# Revit family: Door_Sliding_AssaAbloy_Resilience-FBO-Single-MS
name_source: partatom
category: Doors
revit_build: Autodesk Revit 2016 (Build: 20150714_1515(x64)
units: mm (PartAtom-declared; Revit-internal decimal feet)

## family parameters
Always vertical = Yes
Cut with Voids When Loaded = No
Host = Wall
OmniClass Number = 23.30.10.17.11
OmniClass Title = Sliding Doors
Room Calculation Point = No
Shared = No

## types (14) — shared parameters
AAMA Designation = DP 80
Analytic Construction = <None>
Assembly Code = B2030110
Exit Device Height = 3' - 0"
Fire Rating = As Specified
Fixed Sidelight = Yes
Frame Depth = 0' - 4 1/2"
Full Breakout = No
Function = Interior
Heat Transfer Coefficient (U) = 0.1 BTU/(h·ft²·°F)
Jamb Width = 0' - 1 3/4"
Keynote = 08463
Manufacturer = ASSA ABLOY Entrance Systems
Maximum Size = 86 W x 90 H -- 108 W x 104 H
Medium Stile = Yes
Muntin Width Options = 1-3/4'', 4''
Narrow Stile = No
Panel Thickness = 0' - 1 3/4"
R = 0.0000 (h·ft²·°F)/BTU
RO Offset = 0' - 0 1/4"
Stile Width = 0' - 4"
Thermal Resistance (R) = 0.0000 (h·ft²·°F)/BTU
Thickness = 0' - 0"
U = 0.1 BTU/(h·ft²·°F)
URL = https://www.assaabloyentrance.us
Wall Closure = By host
Water Penetration = NOT TESTED OR RATED for Water Infiltration
zero-valued in all types: Expected Lifespan (Years), Maintenance Schedule (Months), SHGC, Solar Heat Gain Coefficient, VLT, Visual Light Transmittance, Warranty Duration (Years)

## per-type parameters (varying)
| type | Description | Include Muntin A | Include Muntin B | Include Muntin C | Model | Muntin Width | Standards Conformance |
| Category D - No Muntins | ASSA ABLOY Automatic Impact Rated Sliding Door - SL500 Resilience R104 D as Specified | No | No | No | ASSA ABLOY SS SL500 Resilience R104 D Medium Stile | 0' - 1 3/4" | State of Florida FL26008  ;  Category D Impact 50 FPS |
| Category D - 1.75'' Muntin 41.25'' AFF | ASSA ABLOY Automatic Impact Rated Sliding Door - SL500 Resilience R104 D as Specified | Yes | No | No | ASSA ABLOY SS SL500 Resilience R104 D Medium Stile | 0' - 1 3/4" | State of Florida FL26008  ;  Category D Impact 50 FPS |
| Category D - 1.75'' Muntin 42'' AFF | ASSA ABLOY Automatic Impact Rated Sliding Door - SL500 Resilience R104 D as Specified | No | Yes | No | ASSA ABLOY SS SL500 Resilience R104 D Medium Stile | 0' - 1 3/4" | State of Florida FL26008  ;  Category D Impact 50 FPS |
| Category D - 4'' Muntin 41.25'' AFF | ASSA ABLOY Automatic Impact Rated Sliding Door - SL500 Resilience R104 D as Specified | Yes | No | No | ASSA ABLOY SS SL500 Resilience R104 D Medium Stile | 0' - 4" | State of Florida FL26008  ;  Category D Impact 50 FPS |
| Category D - 4'' Muntin 42'' AFF | ASSA ABLOY Automatic Impact Rated Sliding Door - SL500 Resilience R104 D as Specified | No | Yes | No | ASSA ABLOY SS SL500 Resilience R104 D Medium Stile | 0' - 4" | State of Florida FL26008  ;  Category D Impact 50 FPS |
| Category D - Dual 1.75'' Muntin 24'' and 42'' AFF | ASSA ABLOY Automatic Impact Rated Sliding Door - SL500 Resilience R104 D as Specified | No | Yes | Yes | ASSA ABLOY SS SL500 Resilience R104 D Medium Stile | 0' - 1 3/4" | State of Florida FL26008  ;  Category D Impact 50 FPS |
| Category D - Dual 4'' Muntin 24'' and 42'' AFF | ASSA ABLOY Automatic Impact Rated Sliding Door - SL500 Resilience R104 D as Specified | No | Yes | Yes | ASSA ABLOY SS SL500 Resilience R104 D Medium Stile | 0' - 4" | State of Florida FL26008  ;  Category D Impact 50 FPS |
| Category E - No Muntins | ASSA ABLOY Automatic Impact Rated Sliding Door - SL500 Resilience R104 E as Specified | No | No | No | ASSA ABLOY SS SL500 Resilience R104 E Medium Stile | 0' - 1 3/4" | State of Florida FL26008  ;  Category E Impact 80 FPS |
| Category E - 1.75'' Muntin 41.25'' AFF | ASSA ABLOY Automatic Impact Rated Sliding Door - SL500 Resilience R104 E as Specified | Yes | No | No | ASSA ABLOY SS SL500 Resilience R104 E Medium Stile | 0' - 1 3/4" | State of Florida FL26008  ;  Category E Impact 80 FPS |
| Category E - 1.75'' Muntin 42'' AFF | ASSA ABLOY Automatic Impact Rated Sliding Door - SL500 Resilience R104 E as Specified | No | Yes | No | ASSA ABLOY SS SL500 Resilience R104 E Medium Stile | 0' - 1 3/4" | State of Florida FL26008  ;  Category E Impact 80 FPS |
| Category E - 4'' Muntin 41.25'' AFF | ASSA ABLOY Automatic Impact Rated Sliding Door - SL500 Resilience R104 E as Specified | Yes | No | No | ASSA ABLOY SS SL500 Resilience R104 E Medium Stile | 0' - 4" | State of Florida FL26008  ;  Category E Impact 80 FPS |
| Category E - 4'' Muntin 42'' AFF | ASSA ABLOY Automatic Impact Rated Sliding Door - SL500 Resilience R104 E as Specified | No | Yes | No | ASSA ABLOY SS SL500 Resilience R104 E Medium Stile | 0' - 4" | State of Florida FL26008  ;  Category E Impact 80 FPS |
| Category E - Dual 1.75'' Muntin 24'' and 42'' AFF | ASSA ABLOY Automatic Impact Rated Sliding Door - SL500 Resilience R104 E as Specified | No | Yes | Yes | ASSA ABLOY SS SL500 Resilience R104 E Medium Stile | 0' - 1 3/4" | State of Florida FL26008  ;  Category E Impact 80 FPS |
| Category E - Dual 4'' Muntin 24'' and 42'' AFF | ASSA ABLOY Automatic Impact Rated Sliding Door - SL500 Resilience R104 E as Specified | No | Yes | Yes | ASSA ABLOY SS SL500 Resilience R104 E Medium Stile | 0' - 4" | State of Florida FL26008  ;  Category E Impact 80 FPS |

## geometry (parser evidence)
native form markers: Sweep x16
no freeform markers — native parametric forms only
